# Revit family: CENTUM Massivanschluss hängend
name_source: partatom
category: HLS-Bauteile
revit_build: Autodesk Revit 2017 (Build: 20190507_1515(x64)
units: mm (PartAtom-declared; Revit-internal decimal feet)

## family parameters
Arbeitsebenenbasiert = Ja
Beim Laden mit Abzugskörper schneiden = Nein
Bemaßung runder Anschluss = Durchmesser verwenden
Gemeinsam genutzt = Ja
Immer vertikal = Nein
Raumberechnungspunkt = Nein
Teiletyp = Normal

## types (7) — shared parameters
Anzahl Befestigungsloch = 4 St
B = 101 mm
Fabrikat = MEFA
Firma = MEFA Befestigungs- und Montagesysteme GmbH
H2 = 29 mm
Langloch = 14x40 mm
Länge = 130 mm  [stored 0.426509 ft]
MD = 6 mm  [stored 0.019685 ft]
Material = Stahl
Materialname = S235
Mengeneinheit = St
Oberflaeche = Zink-Nickel
Sicherheitsfaktor = 1.54
Stärke = 6 mm  [stored 0.019685 ft]
Vorgabe-Ansicht = 1219 mm
max. zul. Last = 10.00 kN
vpe = 1 St
zero-valued in all types: Höhe Anschlussplatte

## per-type parameters (varying)
| type | Anschluss | Anschlüssgewinde | Artikelnummer | Breite | EAN | Gewicht | Gewicht pro Bauteil | H | H1 | HGA | Höhe | Höhe bis Lochung | Kurztext1 | Kurztext2 | Profiltyp |
| CENTUM Massivanschluss XL100/XL200, M16, hängend | M16 | 6kt-Mutter parametrik : Mutter M16 (4120522) | 1641019007 | 113 mm  [stored 0.370735 ft] | 4250928437099 | 1.65 kg | 1.65 kg | 86 mm | 51 mm | 15 mm  [stored 0.0492126 ft] | 86 mm | 50 mm | Massivanschluss M16 | für Profiltyp XL 100, XL 200 | XL 100, XL 200 |
| CENTUM Massivanschluss XL100/XL200, 1/2", hängend | 1/2'' | Runde Gewindeanschlusse parametrik : Muffe 1/2´´ (0009865) | 1641019008 | 113 mm  [stored 0.370735 ft] | 4250928437105 | 1.64 kg | 1.64 kg | 86 mm | 51 mm | 15 mm  [stored 0.0492126 ft] | 86 mm | 50 mm | Massivanschluss 1/2" | für Profiltyp XL 100, XL 200 | XL 100, XL 200 |
| CENTUM Massivanschluss XL100/XL200, 1", hängend | 1'' | Runde Gewindeanschlusse parametrik : Muffe 1´´ (0009881) | 1641019010 | 113 mm  [stored 0.370735 ft] | 4250928437112 | 1.69 kg | 1.69 kg | 86 mm | 51 mm | 20 mm  [stored 0.0656168 ft] | 86 mm | 50 mm | Massivanschluss 1" | für Profiltyp XL 100, XL 200 | XL 100, XL 200 |
| CENTUM Massivanschluss XL120, M16, hängend | M16 | 6kt-Mutter parametrik : Mutter M16 (4120522) | 1641219007 | 133 mm  [stored 0.436352 ft] | 4250928437167 | 1.78 kg | 1.78 kg | 96 mm  [stored 0.314961 ft] | 61 mm  [stored 0.200131 ft] | 15 mm  [stored 0.0492126 ft] | 96 mm | 60 mm | Massivanschluss M16 | für Profiltyp XL 120 | XL 120 |
| CENTUM Massivanschluss XL120, 1/2", hängend | 1/2'' | Runde Gewindeanschlusse parametrik : Muffe 1/2´´ (0009865) | 1641219008 | 133 mm  [stored 0.436352 ft] | 4250928437174 | 1.77 kg | 1.77 kg | 96 mm  [stored 0.314961 ft] | 61 mm  [stored 0.200131 ft] | 15 mm  [stored 0.0492126 ft] | 96 mm | 60 mm | Massivanschluss 1/2" | für Profiltyp XL 120 | XL 120 |
| CENTUM Massivanschluss XL120, 1", hängend | 1'' | Runde Gewindeanschlusse parametrik : Muffe 1´´ (0009881) | 1641219010 | 133 mm  [stored 0.436352 ft] | 4250928437181 | 1.82 kg | 1.82 kg | 96 mm  [stored 0.314961 ft] | 61 mm  [stored 0.200131 ft] | 20 mm  [stored 0.0656168 ft] | 96 mm | 60 mm | Massivanschluss 1" | für Profiltyp XL 120 | XL 120 |
| CENTUM Massivanschluss XL100/XL200, 3/4", hängend |  | Runde Gewindeanschlusse parametrik : Schweißmuffe 3/4´´ (0009873) | 1641019009 | 113 mm  [stored 0.370735 ft] |  | 0.00 kg | 0.00 kg | 86 mm | 51 mm | 15 mm  [stored 0.0492126 ft] | 86 mm | 50 mm |  | für Profiltyp XL 100, XL 200 | XL 100, XL 200 |

note: [stored X ft] marks values corroborated as IEEE doubles in the binary element streams (Revit-internal decimal feet)

## geometry (parser evidence)
native form markers: Sweep x6
no freeform markers — native parametric forms only
